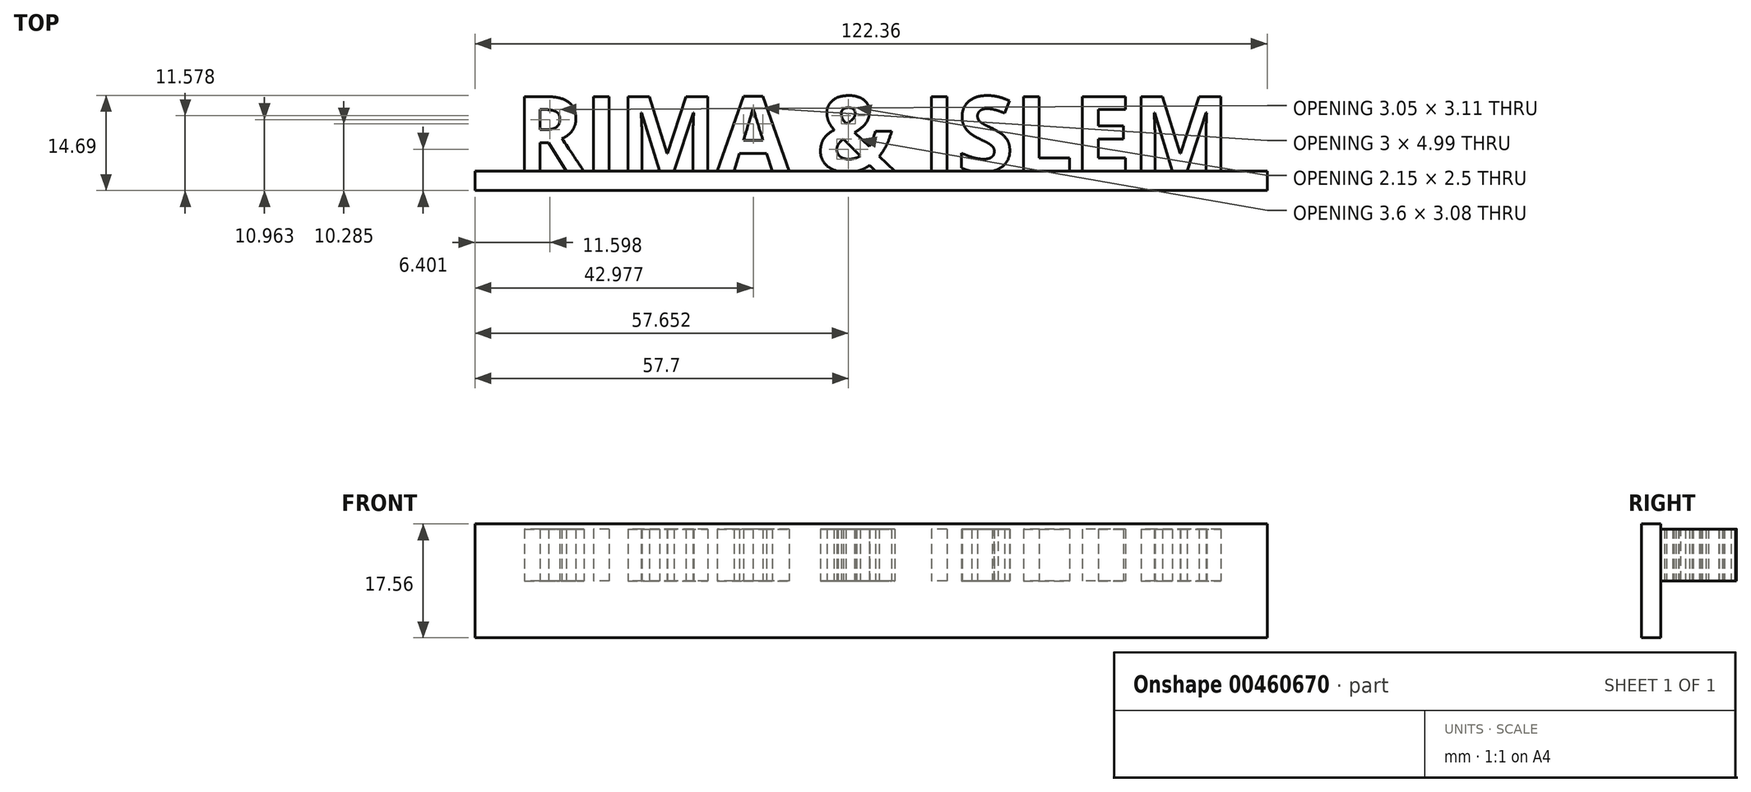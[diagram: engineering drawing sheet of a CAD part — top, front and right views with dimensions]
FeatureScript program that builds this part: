
annotation { "Feature Type Name" : "Feature", "Feature Type Description" : "" }
export const myFeature = defineFeature(function(context is Context, id is Id, definition is map)
    precondition{}
    {
        {
            var Q0;
            Q0=qCreatedBy(makeId("Front.planeOp"),FACE);
            var sketch = newSketch(context, id + "F0", { "sketchPlane" : qUnion([Q0])});
            skLineSegment(sketch, "E0.bottom", {"start": v(61.18, 8.78) * mm, "end": v(-61.18, 8.78) * mm});
            skLineSegment(sketch, "E0.top", {"start": v(61.18, -8.78) * mm, "end": v(-61.18, -8.78) * mm});
            skLineSegment(sketch, "E0.left", {"start": v(61.18, 8.78) * mm, "end": v(61.18, -8.78) * mm});
            skLineSegment(sketch, "E0.right", {"start": v(-61.18, 8.78) * mm, "end": v(-61.18, -8.78) * mm});
            skPoint(sketch, "E0.middle", {"position": v(0, 0) * mm});
            skSolve(sketch);
        }
        {
            var Q0;
            Q0=makeQuery(id+"F0.imprint","IMPRINT",FACE,{"disambiguationData":[TD([[makeQuery(id+"F0.imprint","IMPRINT",EDGE,{"derivedFrom":sQuery(id+"F0.wireOp",EDGE,"E0.bottom")}),1.0]])]});
            extrude(context, id + "F1", {"entities" : qUnion([Q0]), "depth" : 3 * mm});
        }
        {
            var Q0;
            Q0=qCreatedBy(makeId("Top.planeOp"),FACE);
            var sketch = newSketch(context, id + "F2", { "sketchPlane" : qUnion([Q0])});
            skText(sketch, "E1", { "text": "RIMA & ISLEM", "fontName": "OpenSans-Bold.ttf"});
            const initialGuessF2  = {"E1": [-0.055, 0, 1, 0, 0.01162]};
            skSetInitialGuess(sketch, initialGuessF2);
            skSolve(sketch);
        }
        {
            var Q0;
            Q0 = qSketchRegion(id + "F2", true);
            extrude(context, id + "F3", {"entities" : qUnion([Q0]), "operationType" : NewBodyOperationType.ADD, "depth" : 8 * mm});
        }
    });
